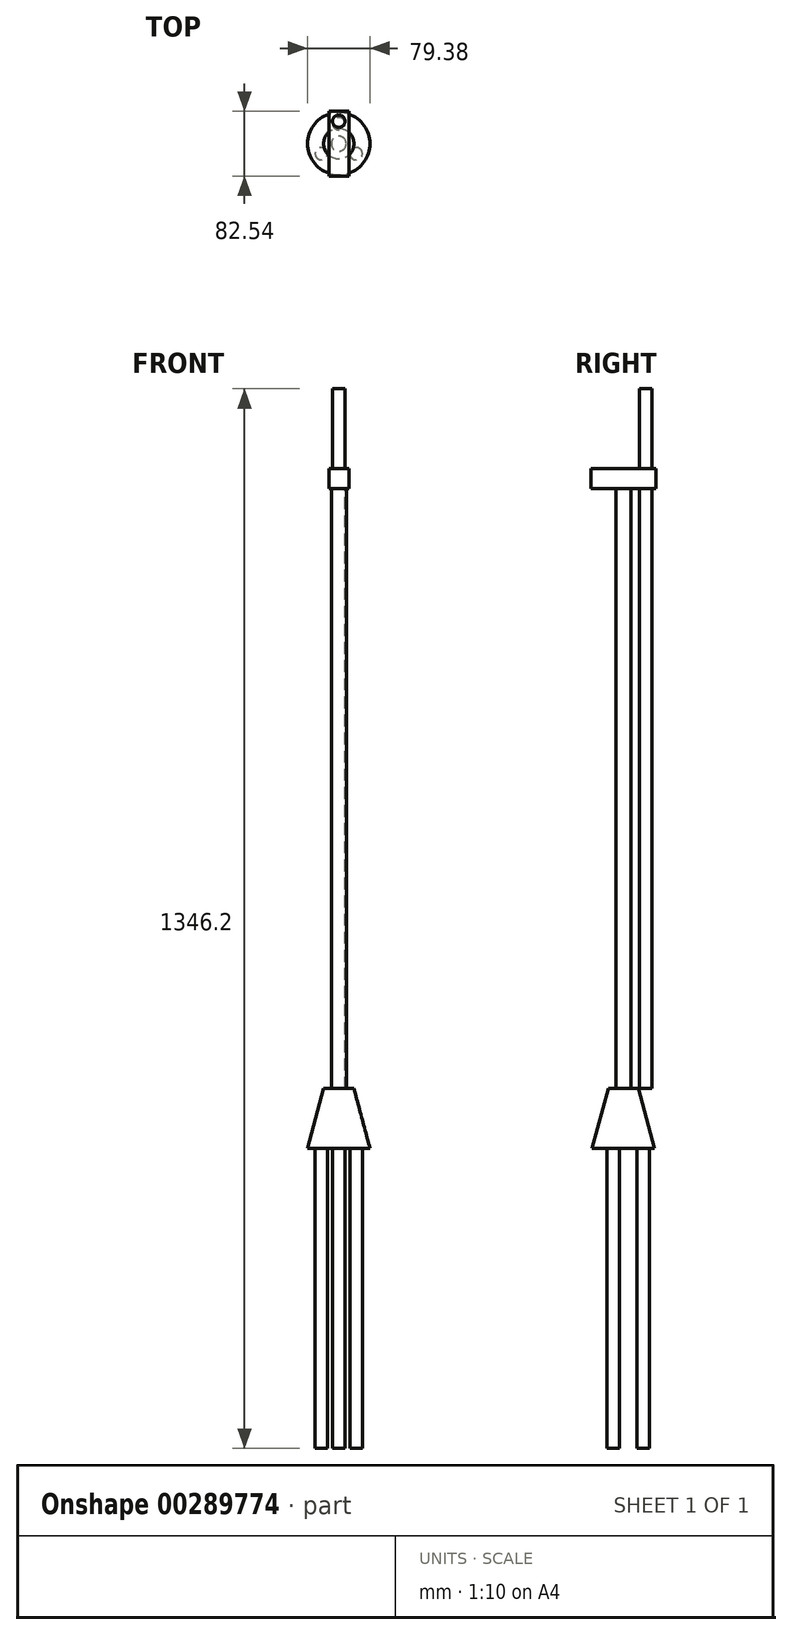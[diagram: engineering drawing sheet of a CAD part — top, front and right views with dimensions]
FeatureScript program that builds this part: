
annotation { "Feature Type Name" : "Feature", "Feature Type Description" : "" }
export const myFeature = defineFeature(function(context is Context, id is Id, definition is map)
    precondition{}
    {
        {
            var Q0;
            Q0=qCreatedBy(makeId("Top.planeOp"),FACE);
            var sketch = newSketch(context, id + "F0", { "sketchPlane" : qUnion([Q0])});
            skCircle(sketch, "E0", {"center": v(0, 25.4) * mm, "radius": 7.94 * mm});
            skCircle(sketch, "E1.1.0", {"center": v(-22, -12.7) * mm, "radius": 7.94 * mm});
            skCircle(sketch, "E1.2.0", {"center": v(22, -12.7) * mm, "radius": 7.94 * mm});
            skPoint(sketch, "E1.center", {"position": v(0, 0) * mm});
            skCircle(sketch, "E2", {"center": v(0, 0) * mm, "radius": 25.4 * mm, "construction": true});
            skSolve(sketch);
        }
        {
            var Q0;
            Q0 = qSketchRegion(id + "F0", true);
            extrude(context, id + "F1", {"entities" : qUnion([Q0]), "depth" : 381 * mm});
        }
        {
            var Q0;
            Q0=makeQuery(id+"F1.opExtrude","CAP_FACE",FACE,{"disambiguationData":[OSD([sQuery(id+"F0.wireOp",EDGE,"E1.1.0")])],"isStart":false});
            var sketch = newSketch(context, id + "F2", { "sketchPlane" : qUnion([Q0])});
            skCircle(sketch, "E3", {"center": v(0, 0) * mm, "radius": 39.69 * mm});
            skCircle(sketch, "E4.0", {"center": v(0, 25.4) * mm, "radius": 7.94 * mm, "construction": true});
            skSolve(sketch);
        }
        {
            var Q0;
            Q0=makeQuery(id+"F2.imprint","IMPRINT",FACE,{"disambiguationData":[TD([[makeQuery(id+"F2.imprint","IMPRINT",EDGE,{"derivedFrom":sQuery(id+"F2.wireOp",EDGE,"E3")}),1.0]])]});
            var Q1;
            Q1=makeQuery(id+"F2.imprint","IMPRINT",FACE,{"disambiguationData":[TD([[makeQuery(id+"F2.imprint","IMPRINT",EDGE,{"derivedFrom":makeQuery(id+"F1.opExtrude","CAP_EDGE",EDGE,{"disambiguationData":[OSD([sQuery(id+"F0.wireOp",EDGE,"E1.1.0")])],"isStart":false})}),1.0]])]});
            extrude(context, id + "F3", {"entities" : qUnion([Q0, Q1]), "depth" : 76.2 * mm, "hasDraft" : true, "draftAngle" : 15 * degree, "draftPullDirection" : true});
        }
        {
            var Q0;
            Q0=makeQuery(id+"F3.opExtrude","CAP_FACE",FACE,{"disambiguationData":[OSD([sQuery(id+"F2.wireOp",EDGE,"E3")])],"isStart":false});
            var sketch = newSketch(context, id + "F4", { "sketchPlane" : qUnion([Q0])});
            skCircle(sketch, "E5", {"center": v(0, 0) * mm, "radius": 9.53 * mm});
            skSolve(sketch);
        }
        {
            var Q0;
            Q0=makeQuery(id+"F4.imprint","IMPRINT",FACE,{"disambiguationData":[TD([[makeQuery(id+"F4.imprint","IMPRINT",EDGE,{"derivedFrom":sQuery(id+"F4.wireOp",EDGE,"E5")}),1.0]])]});
            extrude(context, id + "F5", {"entities" : qUnion([Q0]), "depth" : 762 * mm});
        }
        {
            var Q0;
            Q0=makeQuery(id+"F5.opExtrude","CAP_FACE",FACE,{"disambiguationData":[OSD([sQuery(id+"F4.wireOp",EDGE,"E5")])],"isStart":false});
            var sketch = newSketch(context, id + "F6", { "sketchPlane" : qUnion([Q0])});
            skLineSegment(sketch, "E6.bottom", {"start": v(-12.7, 41.28) * mm, "end": v(12.7, 41.28) * mm});
            skLineSegment(sketch, "E6.top", {"start": v(-12.7, -41.28) * mm, "end": v(12.7, -41.28) * mm});
            skLineSegment(sketch, "E6.left", {"start": v(-12.7, 41.28) * mm, "end": v(-12.7, -41.28) * mm});
            skLineSegment(sketch, "E6.right", {"start": v(12.7, 41.28) * mm, "end": v(12.7, -41.28) * mm});
            skPoint(sketch, "E6.middle", {"position": v(0, 0) * mm});
            skSolve(sketch);
        }
        {
            var Q0;
            Q0=makeQuery(id+"F6.imprint","IMPRINT",FACE,{"disambiguationData":[TD([[makeQuery(id+"F6.imprint","IMPRINT",EDGE,{"derivedFrom":sQuery(id+"F6.wireOp",EDGE,"E6.bottom")}),-1.0]])]});
            var Q1;
            Q1=makeQuery(id+"F6.imprint","IMPRINT",FACE,{"disambiguationData":[TD([[makeQuery(id+"F6.imprint","IMPRINT",EDGE,{"derivedFrom":makeQuery(id+"F5.opExtrude","CAP_EDGE",EDGE,{"disambiguationData":[OSD([sQuery(id+"F4.wireOp",EDGE,"E5")])],"isStart":false})}),1.0]])]});
            extrude(context, id + "F7", {"entities" : qUnion([Q0, Q1]), "operationType" : NewBodyOperationType.ADD, "depth" : 25.4 * mm});
        }
        {
            var Q0;
            Q0=makeQuery(id+"F7.opExtrude","CAP_FACE",FACE,{"disambiguationData":[OSD([sQuery(id+"F6.wireOp",EDGE,"E6.bottom"),sQuery(id+"F6.wireOp",EDGE,"E6.top"),sQuery(id+"F6.wireOp",EDGE,"E6.left"),sQuery(id+"F6.wireOp",EDGE,"E6.right")])],"isStart":true});
            var sketch = newSketch(context, id + "F8", { "sketchPlane" : qUnion([Q0])});
            skCircle(sketch, "E7", {"center": v(0, -28.58) * mm, "radius": 7.94 * mm});
            skSolve(sketch);
        }
        {
            var Q0;
            Q0=makeQuery(id+"F8.imprint","IMPRINT",FACE,{"disambiguationData":[TD([[makeQuery(id+"F8.imprint","IMPRINT",EDGE,{"derivedFrom":sQuery(id+"F8.wireOp",EDGE,"E7")}),1.0]])]});
            extrude(context, id + "F9", {"entities" : qUnion([Q0]), "operationType" : NewBodyOperationType.ADD, "depth" : 762 * mm, "hasSecondDirection" : true, "secondDirectionOppositeDirection" : true, "secondDirectionDepth" : 127 * mm});
        }
    });
